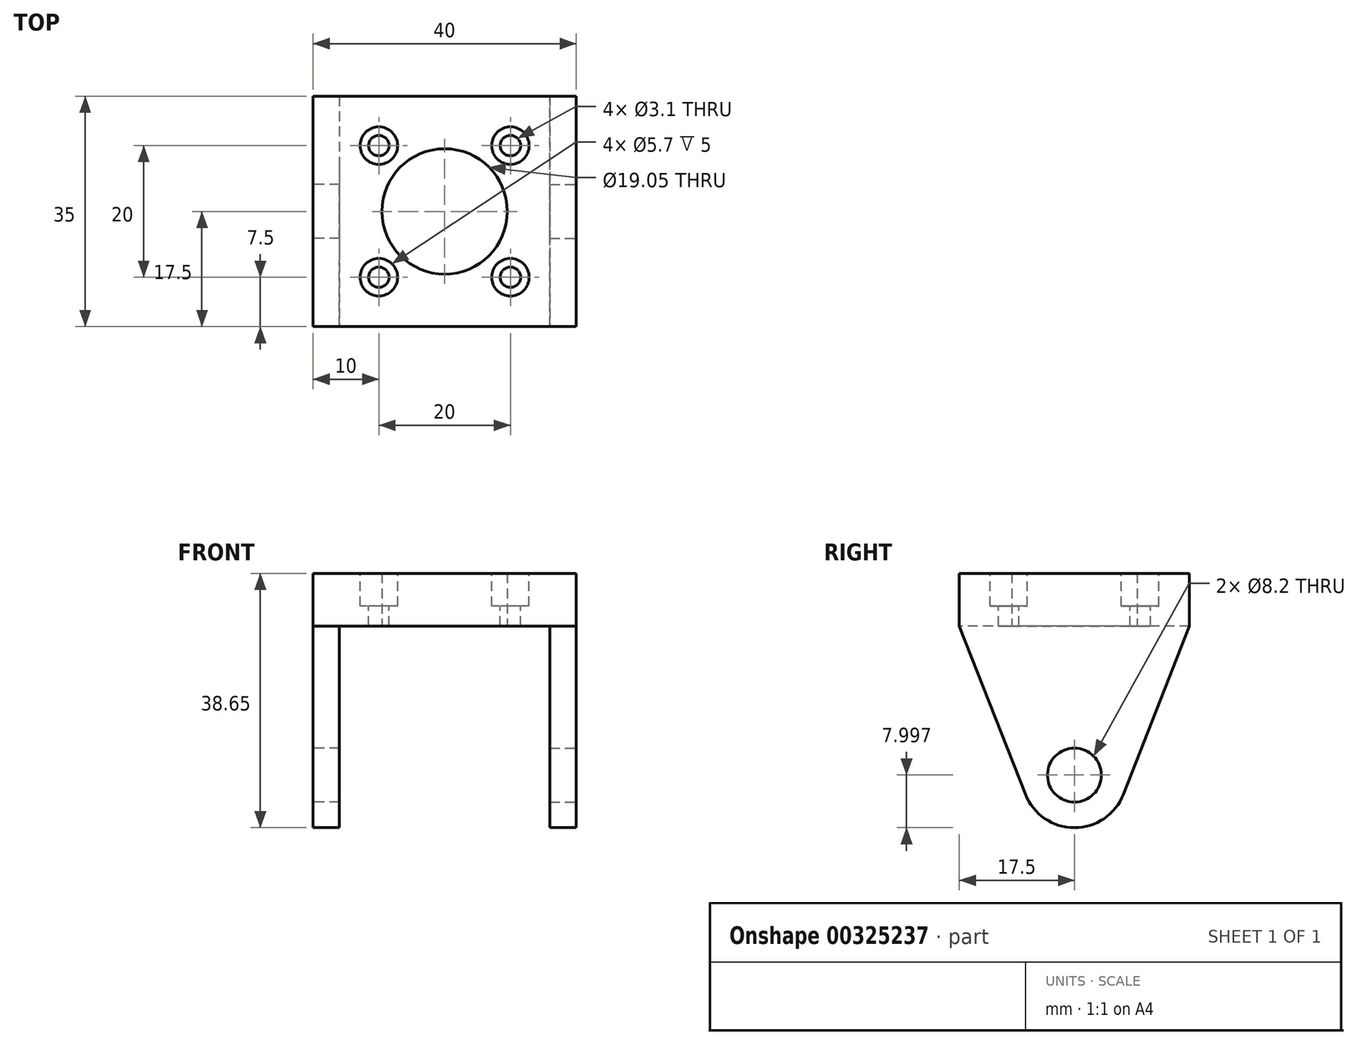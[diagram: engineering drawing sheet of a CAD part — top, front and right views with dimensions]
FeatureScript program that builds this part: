
annotation { "Feature Type Name" : "Feature", "Feature Type Description" : "" }
export const myFeature = defineFeature(function(context is Context, id is Id, definition is map)
    precondition{}
    {
        {
            var Q0;
            Q0=qCreatedBy(makeId("Top.planeOp"),FACE);
            var sketch = newSketch(context, id + "F0", { "sketchPlane" : qUnion([Q0])});
            skLineSegment(sketch, "E0.bottom", {"start": v(20, 17.5) * mm, "end": v(-20, 17.5) * mm});
            skLineSegment(sketch, "E0.top", {"start": v(20, -17.5) * mm, "end": v(-20, -17.5) * mm});
            skLineSegment(sketch, "E0.left", {"start": v(20, 17.5) * mm, "end": v(20, -17.5) * mm});
            skLineSegment(sketch, "E0.right", {"start": v(-20, 17.5) * mm, "end": v(-20, -17.5) * mm});
            skPoint(sketch, "E0.middle", {"position": v(0, 0) * mm});
            skCircle(sketch, "E1", {"center": v(0, 0) * mm, "radius": 9.53 * mm});
            skSolve(sketch);
        }
        {
            var Q0;
            Q0=makeQuery(id+"F0.imprint","IMPRINT",FACE,{"disambiguationData":[TD([[makeQuery(id+"F0.imprint","IMPRINT",EDGE,{"derivedFrom":sQuery(id+"F0.wireOp",EDGE,"E0.bottom")}),1.0]])]});
            extrude(context, id + "F1", {"entities" : qUnion([Q0]), "depth" : 8 * mm});
        }
        {
            var Q0;
            Q0=makeQuery(id+"F1.opExtrude","SWEPT_FACE",FACE,{"disambiguationData":[OSD([sQuery(id+"F0.wireOp",EDGE,"E0.right")])]});
            var sketch = newSketch(context, id + "F2", { "sketchPlane" : qUnion([Q0])});
            skCircle(sketch, "E2", {"center": v(0, -22.65) * mm, "radius": 4.1 * mm});
            skPoint(sketch, "E2.centerSnap0", {"position": v(0, 0) * mm});
            skArc(sketch, "E3", {"start": v(-7.45, -25.58) * mm, "mid": v(0, -30.65) * mm, "end": v(7.45, -25.58) * mm});
            skLineSegment(sketch, "E4", {"start": v(-17.5, 0) * mm, "end": v(-7.45, -25.58) * mm});
            skLineSegment(sketch, "E5", {"start": v(17.5, 0) * mm, "end": v(7.45, -25.58) * mm});
            skSolve(sketch);
        }
        {
            var Q0;
            Q0=makeQuery(id+"F2.imprint","IMPRINT",FACE,{"disambiguationData":[TD([[makeQuery(id+"F2.imprint","IMPRINT",EDGE,{"derivedFrom":sQuery(id+"F2.wireOp",EDGE,"E2")}),-1.0]])]});
            extrude(context, id + "F3", {"entities" : qUnion([Q0]), "operationType" : NewBodyOperationType.ADD, "oppositeDirection" : true, "depth" : 4 * mm});
        }
        {
            var Q0;
            Q0=makeQuery(id+"F1.opExtrude","SWEPT_FACE",FACE,{"disambiguationData":[OSD([sQuery(id+"F0.wireOp",EDGE,"E0.left")])]});
            var sketch = newSketch(context, id + "F4", { "sketchPlane" : qUnion([Q0])});
            skLineSegment(sketch, "E6.0.0", {"start": v(-17.5, 0) * mm, "end": v(-7.45, -25.58) * mm});
            skArc(sketch, "E6.0.1", {"start": v(-7.45, -25.58) * mm, "mid": v(0, -30.65) * mm, "end": v(7.45, -25.58) * mm});
            skLineSegment(sketch, "E6.0.2", {"start": v(7.45, -25.58) * mm, "end": v(17.5, 0) * mm});
            skLineSegment(sketch, "E6.0.3", {"start": v(17.5, 0) * mm, "end": v(-17.5, 0) * mm});
            skCircle(sketch, "E7.0", {"center": v(0, -22.65) * mm, "radius": 4.1 * mm});
            skSolve(sketch);
        }
        {
            var Q0;
            Q0 = qSketchRegion(id + "F4", true);
            extrude(context, id + "F5", {"entities" : qUnion([Q0]), "operationType" : NewBodyOperationType.ADD, "oppositeDirection" : true, "depth" : 4 * mm});
        }
        {
            var Q0;
            Q0=makeQuery(id+"F1.opExtrude","CAP_FACE",FACE,{"disambiguationData":[OSD([sQuery(id+"F0.wireOp",EDGE,"E0.bottom"),sQuery(id+"F0.wireOp",EDGE,"E0.top"),sQuery(id+"F0.wireOp",EDGE,"E0.left"),sQuery(id+"F0.wireOp",EDGE,"E0.right"),sQuery(id+"F0.wireOp",EDGE,"E1")])],"isStart":false});
            var sketch = newSketch(context, id + "F6", { "sketchPlane" : qUnion([Q0])});
            skLineSegment(sketch, "E8", {"start": v(-20, 10) * mm, "end": v(20, 10) * mm, "construction": true});
            skLineSegment(sketch, "E9", {"start": v(-10, 17.5) * mm, "end": v(-10, -17.5) * mm, "construction": true});
            skCircle(sketch, "E10", {"center": v(-10, 10) * mm, "radius": 1.55 * mm});
            skCircle(sketch, "E11", {"center": v(-10, 10) * mm, "radius": 2.85 * mm});
            skCircle(sketch, "E12.0.1.0", {"center": v(-10, -10) * mm, "radius": 1.55 * mm});
            skCircle(sketch, "E12.0.1.1", {"center": v(-10, -10) * mm, "radius": 2.85 * mm});
            skCircle(sketch, "E12.1.0.0", {"center": v(10, 10) * mm, "radius": 1.55 * mm});
            skCircle(sketch, "E12.1.0.1", {"center": v(10, 10) * mm, "radius": 2.85 * mm});
            skCircle(sketch, "E12.1.1.0", {"center": v(10, -10) * mm, "radius": 1.55 * mm});
            skCircle(sketch, "E12.1.1.1", {"center": v(10, -10) * mm, "radius": 2.85 * mm});
            skLineSegment(sketch, "E12.direction1", {"start": v(-10, 10) * mm, "end": v(10, 10) * mm, "construction": true});
            skLineSegment(sketch, "E12.direction2", {"start": v(-10, 10) * mm, "end": v(-10, -10) * mm, "construction": true});
            skSolve(sketch);
        }
        {
            var Q0;
            Q0=makeQuery(id+"F6.imprint","IMPRINT",FACE,{"disambiguationData":[TD([[makeQuery(id+"F6.imprint","IMPRINT",EDGE,{"derivedFrom":sQuery(id+"F6.wireOp",EDGE,"E10")}),1.0]])]});
            var Q1;
            Q1=makeQuery(id+"F6.imprint","IMPRINT",FACE,{"disambiguationData":[TD([[makeQuery(id+"F6.imprint","IMPRINT",EDGE,{"derivedFrom":sQuery(id+"F6.wireOp",EDGE,"E12.1.0.0")}),1.0]])]});
            var Q2;
            Q2=makeQuery(id+"F6.imprint","IMPRINT",FACE,{"disambiguationData":[TD([[makeQuery(id+"F6.imprint","IMPRINT",EDGE,{"derivedFrom":sQuery(id+"F6.wireOp",EDGE,"E12.0.1.0")}),1.0]])]});
            var Q3;
            Q3=makeQuery(id+"F6.imprint","IMPRINT",FACE,{"disambiguationData":[TD([[makeQuery(id+"F6.imprint","IMPRINT",EDGE,{"derivedFrom":sQuery(id+"F6.wireOp",EDGE,"E12.1.1.0")}),1.0]])]});
            extrude(context, id + "F7", {"entities" : qUnion([Q0, Q1, Q2, Q3]), "operationType" : NewBodyOperationType.REMOVE, "endBound" : BoundingType.UP_TO_NEXT, "oppositeDirection" : true, "depth" : 25 * mm});
        }
        {
            var Q0;
            Q0 = qSketchRegion(id + "F6", true);
            extrude(context, id + "F8", {"entities" : qUnion([Q0]), "operationType" : NewBodyOperationType.REMOVE, "oppositeDirection" : true, "depth" : 5 * mm});
        }
    });
